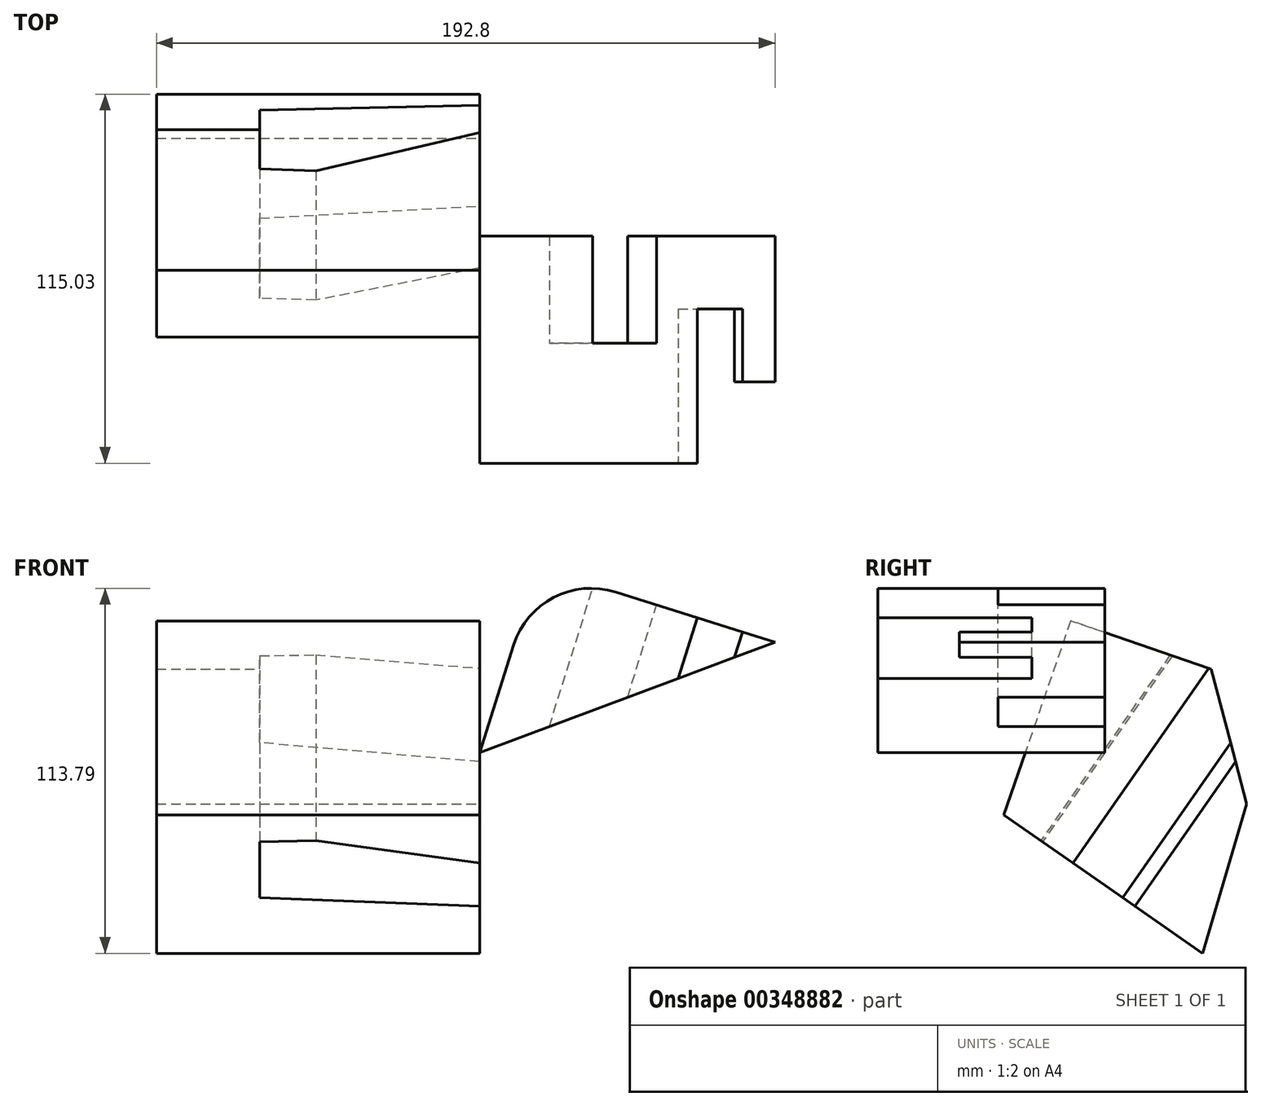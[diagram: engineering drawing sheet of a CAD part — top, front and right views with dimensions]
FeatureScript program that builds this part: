
annotation { "Feature Type Name" : "Feature", "Feature Type Description" : "" }
export const myFeature = defineFeature(function(context is Context, id is Id, definition is map)
    precondition{}
    {
        {
            var Q0;
            Q0=qCreatedBy(makeId("Front.planeOp"),FACE);
            var sketch = newSketch(context, id + "F0", { "sketchPlane" : qUnion([Q0])});
            skLineSegment(sketch, "E0", {"start": v(92.09, 34.5) * mm, "end": v(0, 0) * mm});
            skLineSegment(sketch, "E1", {"start": v(0, 0) * mm, "end": v(18.25, 57.7) * mm});
            skLineSegment(sketch, "E2", {"start": v(18.25, 57.7) * mm, "end": v(92.09, 34.5) * mm});
            skSolve(sketch);
        }
        {
            var Q0;
            Q0=makeQuery(id+"F0.imprint","IMPRINT",FACE,{"disambiguationData":[TD([[makeQuery(id+"F0.imprint","IMPRINT",EDGE,{"derivedFrom":sQuery(id+"F0.wireOp",EDGE,"E0")}),-1.0]])]});
            extrude(context, id + "F1", {"entities" : qUnion([Q0]), "depth" : 45.37 * mm});
        }
        {
            var Q0;
            Q0=makeQuery(id+"F1.opExtrude","SWEPT_FACE",FACE,{"disambiguationData":[OSD([sQuery(id+"F0.wireOp",EDGE,"E2")])]});
            var sketch = newSketch(context, id + "F2", { "sketchPlane" : qUnion([Q0])});
            skLineSegment(sketch, "E3.bottom", {"start": v(18.28, -33.32) * mm, "end": v(38.81, -33.32) * mm});
            skLineSegment(sketch, "E3.top", {"start": v(18.28, 0) * mm, "end": v(38.81, 0) * mm});
            skLineSegment(sketch, "E3.left", {"start": v(18.28, -33.32) * mm, "end": v(18.28, 0) * mm});
            skLineSegment(sketch, "E3.right", {"start": v(38.81, -33.32) * mm, "end": v(38.81, 0) * mm});
            skPoint(sketch, "E4.oppositeSnap0", {"position": v(77.5, -22.68) * mm});
            skLineSegment(sketch, "E4.bottom", {"start": v(66.87, -45.37) * mm, "end": v(52.11, -45.37) * mm});
            skLineSegment(sketch, "E4.top", {"start": v(66.87, -22.68) * mm, "end": v(52.11, -22.68) * mm});
            skLineSegment(sketch, "E4.left", {"start": v(66.87, -45.37) * mm, "end": v(66.87, -22.68) * mm});
            skLineSegment(sketch, "E4.right", {"start": v(52.11, -45.37) * mm, "end": v(52.11, -22.68) * mm});
            skSolve(sketch);
        }
        {
            var Q0;
            Q0=makeQuery(id+"F2.imprint","IMPRINT",FACE,{"disambiguationData":[TD([[makeQuery(id+"F2.imprint","IMPRINT",EDGE,{"derivedFrom":sQuery(id+"F2.wireOp",EDGE,"E3.bottom")}),1.0]])]});
            var Q1;
            Q1=makeQuery(id+"F2.imprint","IMPRINT",FACE,{"disambiguationData":[TD([[makeQuery(id+"F2.imprint","IMPRINT",EDGE,{"derivedFrom":sQuery(id+"F2.wireOp",EDGE,"E4.bottom")}),1.0]])]});
            extrude(context, id + "F3", {"entities" : qUnion([Q0, Q1]), "operationType" : NewBodyOperationType.REMOVE, "oppositeDirection" : true, "depth" : 93.05 * mm});
        }
        {
            var Q0;
            Q0=makeQuery(id+"F1.opExtrude","SWEPT_EDGE",EDGE,{"disambiguationData":[OSD([sQuery(id+"F0.wireOp",EDGE,"E1"),sQuery(id+"F0.wireOp",EDGE,"E2")])]});
            fillet(context, id + "F4", {"entities" : qUnion([Q0]), "radius" : 25.4 * mm, "tangentPropagation" : true, "allowEdgeOverflow" : false});
        }
        {
            var Q0;
            {var subQ0=sQuery(id+"F0.wireOp",EDGE,"E0");var subQ1=sQuery(id+"F0.wireOp",EDGE,"E1");var subQ2=sQuery(id+"F0.wireOp",EDGE,"E2");Q0=makeQuery(id+"F3.boolean.opBoolean","SPLIT",FACE,{"disambiguationData":[TD([makeQuery(id+"F1.opExtrude","SWEPT_FACE",FACE,{"disambiguationData":[OSD([subQ1])]})])],"derivedFrom":makeQuery(id+"F1.opExtrude","CAP_FACE",FACE,{"disambiguationData":[OSD([subQ0,subQ1,subQ2])],"isStart":false})});}
            extrude(context, id + "F5", {"entities" : qUnion([Q0]), "operationType" : NewBodyOperationType.ADD, "depth" : 25.4 * mm});
        }
        {
            var Q0;
            Q0=qCreatedBy(makeId("Right.planeOp"),FACE);
            var sketch = newSketch(context, id + "F6", { "sketchPlane" : qUnion([Q0])});
            skLineSegment(sketch, "E5", {"start": v(33.2, 26.06) * mm, "end": v(-10.64, 41.12) * mm});
            skLineSegment(sketch, "E6", {"start": v(-10.64, 41.12) * mm, "end": v(-31.43, -19.4) * mm});
            skLineSegment(sketch, "E7", {"start": v(-31.43, -19.4) * mm, "end": v(30.53, -62.52) * mm});
            skLineSegment(sketch, "E8", {"start": v(30.53, -62.52) * mm, "end": v(44.26, -15.98) * mm});
            skLineSegment(sketch, "E9", {"start": v(44.26, -15.98) * mm, "end": v(33.2, 26.06) * mm});
            skSolve(sketch);
        }
        {
            var Q0;
            Q0=makeQuery(id+"F6.imprint","IMPRINT",FACE,{"disambiguationData":[TD([[makeQuery(id+"F6.imprint","IMPRINT",EDGE,{"derivedFrom":sQuery(id+"F6.wireOp",EDGE,"E5")}),1.0]])]});
            extrude(context, id + "F7", {"entities" : qUnion([Q0]), "oppositeDirection" : true, "depth" : 100.7 * mm});
        }
        {
            var Q0;
            Q0=makeQuery(id+"F7.opExtrude","SWEPT_FACE",FACE,{"disambiguationData":[OSD([sQuery(id+"F6.wireOp",EDGE,"E7")])]});
            var sketch = newSketch(context, id + "F8", { "sketchPlane" : qUnion([Q0])});
            skLineSegment(sketch, "E10", {"start": v(-68.49, 0) * mm, "end": v(-68.49, -30.4) * mm});
            skLineSegment(sketch, "E11", {"start": v(-68.49, -30.4) * mm, "end": v(11.8, -35.87) * mm});
            skLineSegment(sketch, "E12", {"start": v(11.8, -35.87) * mm, "end": v(7.13, -13.2) * mm});
            skLineSegment(sketch, "E13", {"start": v(7.13, -13.2) * mm, "end": v(-51, 0.69) * mm});
            skLineSegment(sketch, "E14", {"start": v(-51, 0.69) * mm, "end": v(-68.49, 0) * mm});
            skSolve(sketch);
        }
        {
            var Q0;
            {var subQ0=sQuery(id+"F8.wireOp",EDGE,"E12");Q0=makeQuery(id+"F8.imprint","IMPRINT",FACE,{"disambiguationData":[TD([[makeQuery(id+"F8.imprint","IMPRINT",EDGE,{"derivedFrom":subQ0}),1.0]])]});}
            var Q1;
            {var subQ2=sQuery(id+"F8.wireOp",EDGE,"E10");Q1=makeQuery(id+"F8.imprint","IMPRINT",FACE,{"disambiguationData":[TD([[makeQuery(id+"F8.imprint","IMPRINT",EDGE,{"derivedFrom":subQ2}),1.0]])]});}
            extrude(context, id + "F9", {"entities" : qUnion([Q0, Q1]), "operationType" : NewBodyOperationType.REMOVE, "oppositeDirection" : true, "depth" : 137.82 * mm});
        }
    });
